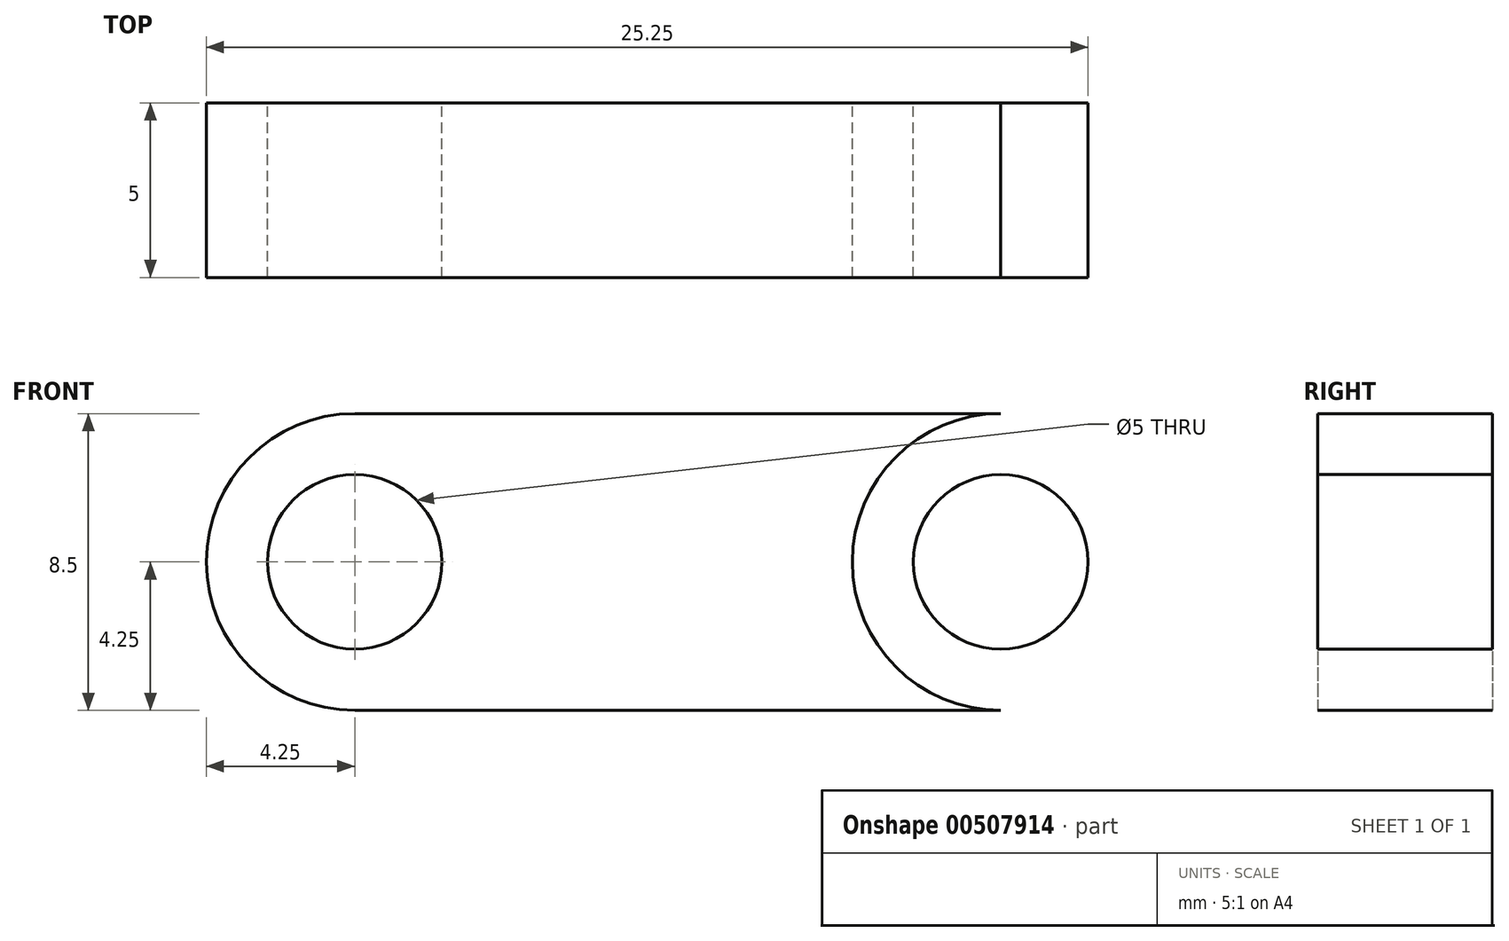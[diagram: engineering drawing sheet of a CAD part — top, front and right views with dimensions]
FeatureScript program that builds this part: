
annotation { "Feature Type Name" : "Feature", "Feature Type Description" : "" }
export const myFeature = defineFeature(function(context is Context, id is Id, definition is map)
    precondition{}
    {
        {
            var Q0;
            Q0=qCreatedBy(makeId("Front.planeOp"),FACE);
            var sketch = newSketch(context, id + "F0", { "sketchPlane" : qUnion([Q0])});
            skLineSegment(sketch, "E0", {"start": v(0, 0) * mm, "end": v(18.5, 0) * mm, "construction": true});
            skLineSegment(sketch, "E1", {"start": v(9.25, 0) * mm, "end": v(9.25, -9.65) * mm, "construction": true});
            skLineSegment(sketch, "E2", {"start": v(9.25, 0) * mm, "end": v(9.25, 8.65) * mm, "construction": true});
            skCircle(sketch, "E3", {"center": v(0, 0) * mm, "radius": 2.5 * mm});
            skCircle(sketch, "E4", {"center": v(0, 0) * mm, "radius": 4.25 * mm});
            skLineSegment(sketch, "E5", {"start": v(0, 4.25) * mm, "end": v(9.25, 4.25) * mm});
            skLineSegment(sketch, "E6", {"start": v(0, -4.25) * mm, "end": v(9.25, -4.25) * mm});
            skLineSegment(sketch, "E7.MirrorCS", {"start": v(18.5, 4.25) * mm, "end": v(9.25, 4.25) * mm});
            skCircle(sketch, "E8.MirrorC", {"center": v(18.5, 0) * mm, "radius": 4.25 * mm});
            skCircle(sketch, "E9.MirrorC", {"center": v(18.5, 0) * mm, "radius": 2.5 * mm});
            skLineSegment(sketch, "E10.MirrorCS", {"start": v(18.5, -4.25) * mm, "end": v(9.25, -4.25) * mm});
            skSolve(sketch);
        }
        {
            var Q0;
            Q0=makeQuery(id+"F0.imprint","IMPRINT",FACE,{"disambiguationData":[TD([[makeQuery(id+"F0.imprint","IMPRINT",EDGE,{"derivedFrom":sQuery(id+"F0.wireOp",EDGE,"E3")}),-1.0]])]});
            var Q1;
            {var subQ2=sQuery(id+"F0.wireOp",EDGE,"E5");Q1=makeQuery(id+"F0.imprint","IMPRINT",FACE,{"disambiguationData":[TD([[makeQuery(id+"F0.imprint","IMPRINT",EDGE,{"derivedFrom":subQ2}),-1.0]])]});}
            var Q2;
            Q2=makeQuery(id+"F0.imprint","IMPRINT",FACE,{"disambiguationData":[TD([[makeQuery(id+"F0.imprint","IMPRINT",EDGE,{"derivedFrom":sQuery(id+"F0.wireOp",EDGE,"E9.MirrorC")}),1.0]])]});
            extrude(context, id + "F1", {"entities" : qUnion([Q0, Q1, Q2]), "depth" : 5 * mm, "offsetDistance" : 25 * mm});
        }
    });
